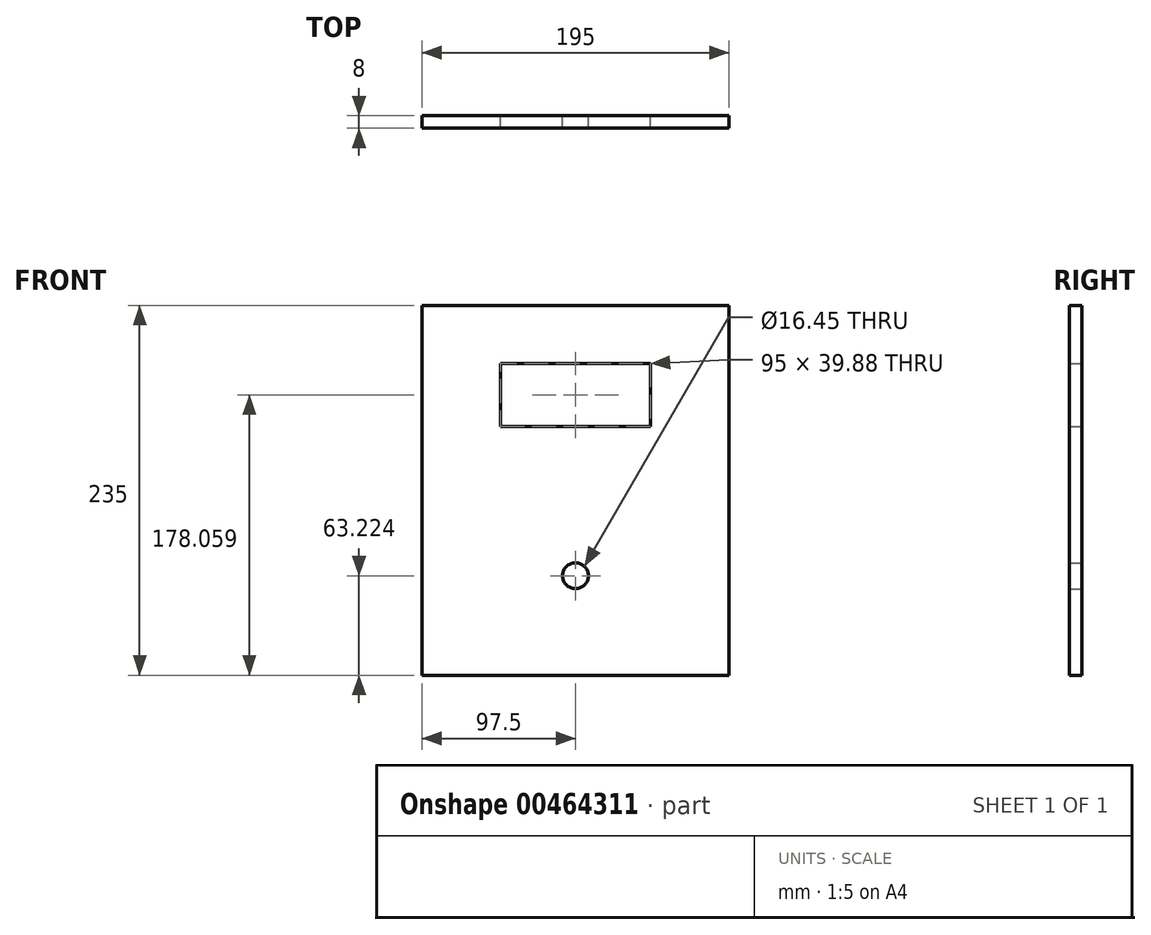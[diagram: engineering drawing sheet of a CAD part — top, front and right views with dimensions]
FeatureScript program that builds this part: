
annotation { "Feature Type Name" : "Feature", "Feature Type Description" : "" }
export const myFeature = defineFeature(function(context is Context, id is Id, definition is map)
    precondition{}
    {
        {
            var Q0;
            Q0=qCreatedBy(makeId("Front.planeOp"),FACE);
            var sketch = newSketch(context, id + "F0", { "sketchPlane" : qUnion([Q0])});
            skLineSegment(sketch, "E0.bottom", {"start": v(-97.5, 117.5) * mm, "end": v(97.5, 117.5) * mm});
            skLineSegment(sketch, "E0.top", {"start": v(-97.5, -117.5) * mm, "end": v(97.5, -117.5) * mm});
            skLineSegment(sketch, "E0.left", {"start": v(-97.5, 117.5) * mm, "end": v(-97.5, -117.5) * mm});
            skLineSegment(sketch, "E0.right", {"start": v(97.5, 117.5) * mm, "end": v(97.5, -117.5) * mm});
            skPoint(sketch, "E0.middle", {"position": v(0, 0) * mm});
            skCircle(sketch, "E1", {"center": v(0, -54.28) * mm, "radius": 8.22 * mm});
            skLineSegment(sketch, "E2.bottom", {"start": v(-47.5, 80.5) * mm, "end": v(47.5, 80.5) * mm});
            skLineSegment(sketch, "E2.top", {"start": v(-47.5, 40.62) * mm, "end": v(47.5, 40.62) * mm});
            skLineSegment(sketch, "E2.left", {"start": v(-47.5, 80.5) * mm, "end": v(-47.5, 40.62) * mm});
            skLineSegment(sketch, "E2.right", {"start": v(47.5, 80.5) * mm, "end": v(47.5, 40.62) * mm});
            skPoint(sketch, "E2.middle", {"position": v(0, 60.56) * mm});
            skSolve(sketch);
        }
        {
            var Q0;
            Q0=makeQuery(id+"F0.imprint","IMPRINT",FACE,{"disambiguationData":[TD([[makeQuery(id+"F0.imprint","IMPRINT",EDGE,{"derivedFrom":sQuery(id+"F0.wireOp",EDGE,"E0.top")}),1.0]])]});
            extrude(context, id + "F1", {"entities" : qUnion([Q0]), "endBound" : BoundingType.SYMMETRIC, "depth" : 8 * mm});
        }
    });
